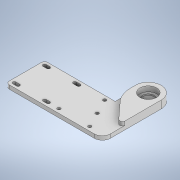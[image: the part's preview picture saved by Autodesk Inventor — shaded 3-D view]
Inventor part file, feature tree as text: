
AUTODESK INVENTOR PART (.ipt)
format: ipt  version: 2020.3 (Build 243373000, 373)  size: 268,288 bytes
history: native  units: mm
features: sketch x5, extrude x4, fillet x4, hole x1
ambient origin geometry x8: Origin, YZ Plane, XZ Plane, XY Plane, X Axis, Y Axis, Z Axis, Center Point
bodies: Solid1 (feature_tree)
feature tree (14):
  sketch  "Sketch1"  dims[d0=40.0mm d1=40.0mm]
  extrude  "Extrusion5"  Depth=6.0mm TaperAngle=0.0deg
  sketch  "Sketch7"  dims[d43=40.0mm d44=40.0mm d45=21.0mm d46=100.0mm d47=34.0mm d48=10.0mm d49=80.0mm d50=40.0mm d51=20.0mm d52=6.0mm d53=0.0mm d64=5.0mm d65=12.5mm]
  fillet  "Fillet10"  Radius=5.0mm
  fillet  "Fillet11"  Radius=12.5mm
  hole  "Hole3"  [1 undecoded]
  extrude  "Extrusion9"  Depth=40.0mm
  extrude  "Extrusion12"  Depth=8.0mm TaperAngle=0.0deg
  extrude  "Extrusion13"  Depth=40.0mm
  fillet  "Fillet13"  Radius=2.0mm
  fillet  "Fillet14"  Radius=4.0mm
  sketch  "Sketch10"  dims[d66=10.0mm d67=24.0mm d68=24.0mm d69=24.0mm d70=40.0mm d72=360.0deg]
  sketch  "Sketch11"  dims[d74=5.0mm d75=6.0mm d76=4.0mm d77=2.0mm d78=90.0deg d79=8.0mm d80=20.594885mm d81=4.22mm]
  sketch  "Sketch12"  dims[d83=6.0mm d84=0.0mm d89=26.0mm d90=8.0mm d91=0.0mm d92=18.0mm d93=2.0mm d94=0.0mm d96=4.0mm d97=40.0mm d21=0.5mm d22=0.872665mm d23=0.5mm d24=0.872665mm d85=0.5mm d86=0.872665mm]
note: 1 required parameter value undecoded (feature->parameter linkage not recoverable at this tier; creation-order binding heuristic only, values carry confidence <= 0.55)
